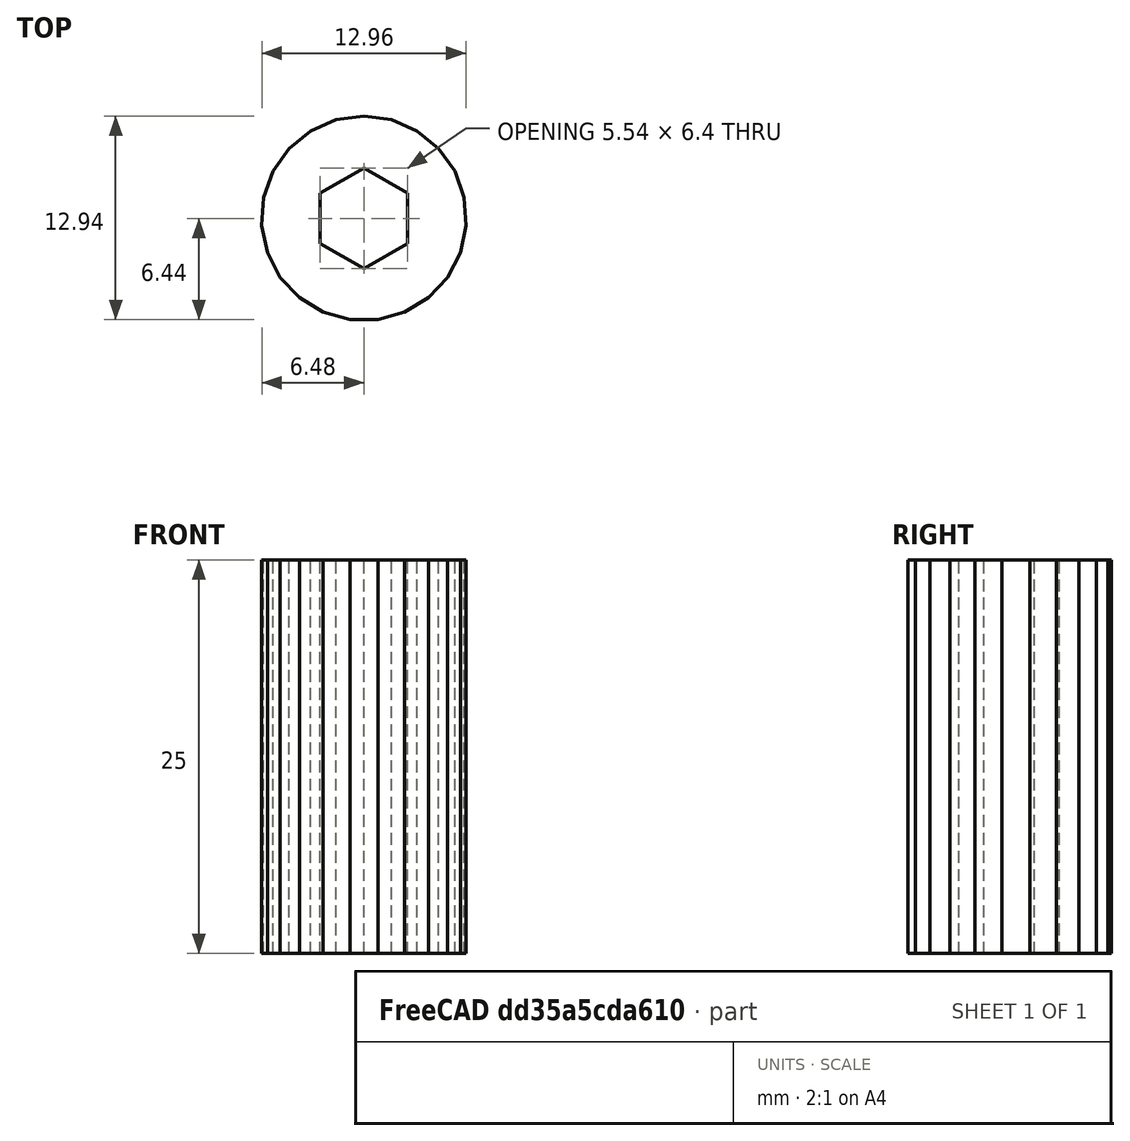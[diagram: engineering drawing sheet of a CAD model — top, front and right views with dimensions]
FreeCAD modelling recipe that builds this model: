
FCSTD DOCUMENT  (FreeCAD 0.19R24344 (Git))
Label: MicroManipulator_Handle
License: All rights reserved
LicenseURL: http://en.wikipedia.org/wiki/All_rights_reserved
objects: Sketcher::SketchObject×1, PartDesign::Pad×1, PartDesign::CoordinateSystem×1, PartDesign::Body×1
note: 5 computed .brp shape members not serialized (recipe doc carries the construction recipe); baked Part::Feature solids carry a one-line shape summary decoded from their .brp

FEATURE [Sketcher::SketchObject] Sketch
  FullyConstrained = true
  MapMode = 5
  Support = -> [XY_Plane]
  sketch-geometry (31):
    g0: LineSegment StartX=2.77128 StartY=-1.6 StartZ=0 EndX=2.77128 EndY=1.6 EndZ=0
    g1: LineSegment StartX=2.77128 StartY=1.6 StartZ=0 EndX=0 EndY=3.2 EndZ=0
    g2: LineSegment StartX=0 StartY=3.2 StartZ=0 EndX=-2.77128 EndY=1.6 EndZ=0
    g3: LineSegment StartX=-2.77128 StartY=1.6 StartZ=0 EndX=-2.77128 EndY=-1.6 EndZ=0
    g4: LineSegment StartX=-2.77128 StartY=-1.6 StartZ=0 EndX=0 EndY=-3.2 EndZ=0
    g5: LineSegment StartX=0 StartY=-3.2 StartZ=0 EndX=2.77128 EndY=-1.6 EndZ=0
    g6: Circle CenterX=0 CenterY=0 CenterZ=0 NormalX=0 NormalY=0 NormalZ=1 AngleXU=0 Radius=3.2
    g7: LineSegment StartX=4.75043 StartY=4.4366 StartZ=0 EndX=3.3773 EndY=5.55373 EndZ=0
    g8: LineSegment StartX=3.3773 StartY=5.55373 StartZ=0 EndX=1.75368 EndY=6.25896 EndZ=0
    g9: LineSegment StartX=1.75368 StartY=6.25896 StartZ=0 EndX=0 EndY=6.5 EndZ=0
    g10: LineSegment StartX=0 StartY=6.5 StartZ=0 EndX=-1.75368 EndY=6.25896 EndZ=0
    g11: LineSegment StartX=-1.75368 StartY=6.25896 StartZ=0 EndX=-3.3773 EndY=5.55373 EndZ=0
    g12: LineSegment StartX=-3.3773 StartY=5.55373 StartZ=0 EndX=-4.75043 EndY=4.4366 EndZ=0
    g13: LineSegment StartX=-4.75043 StartY=4.4366 StartZ=0 EndX=-5.77125 EndY=2.99042 EndZ=0
    g14: LineSegment StartX=-5.77125 StartY=2.99042 StartZ=0 EndX=-6.36405 EndY=1.32246 EndZ=0
    g15: LineSegment StartX=-6.36405 StartY=1.32246 StartZ=0 EndX=-6.48485 EndY=-0.443576 EndZ=0
    g16: LineSegment StartX=-6.48485 StartY=-0.443576 StartZ=0 EndX=-6.1247 EndY=-2.17672 EndZ=0
    g17: LineSegment StartX=-6.1247 StartY=-2.17672 StartZ=0 EndX=-5.3103 EndY=-3.74842 EndZ=0
    g18: LineSegment StartX=-5.3103 StartY=-3.74842 StartZ=0 EndX=-4.10207 EndY=-5.04212 EndZ=0
    g19: LineSegment StartX=-4.10207 StartY=-5.04212 StartZ=0 EndX=-2.58961 EndY=-5.96187 EndZ=0
    g20: LineSegment StartX=-2.58961 StartY=-5.96187 StartZ=0 EndX=-0.885083 EndY=-6.43946 EndZ=0
    g21: LineSegment StartX=-0.885083 StartY=-6.43946 StartZ=0 EndX=0.885083 EndY=-6.43946 EndZ=0
    g22: LineSegment StartX=0.885083 StartY=-6.43946 StartZ=0 EndX=2.58961 EndY=-5.96187 EndZ=0
    g23: LineSegment StartX=2.58961 StartY=-5.96187 StartZ=0 EndX=4.10207 EndY=-5.04212 EndZ=0
    g24: LineSegment StartX=4.10207 StartY=-5.04212 StartZ=0 EndX=5.3103 EndY=-3.74842 EndZ=0
    g25: LineSegment StartX=5.3103 StartY=-3.74842 StartZ=0 EndX=6.1247 EndY=-2.17672 EndZ=0
    g26: LineSegment StartX=6.1247 StartY=-2.17672 StartZ=0 EndX=6.48485 EndY=-0.443576 EndZ=0
    g27: LineSegment StartX=6.48485 StartY=-0.443576 StartZ=0 EndX=6.36405 EndY=1.32246 EndZ=0
    g28: LineSegment StartX=6.36405 StartY=1.32246 StartZ=0 EndX=5.77125 EndY=2.99042 EndZ=0
    g29: LineSegment StartX=5.77125 StartY=2.99042 StartZ=0 EndX=4.75043 EndY=4.4366 EndZ=0
    g30: Circle CenterX=0 CenterY=0 CenterZ=0 NormalX=0 NormalY=0 NormalZ=1 AngleXU=0 Radius=6.5
  constraints (66):
    c: Coincident(g0,g1)
    c: Coincident(g1,g2)
    c: Coincident(g2,g3)
    c: Coincident(g3,g4)
    c: Coincident(g4,g5)
    c: Coincident(g5,g0)
    c: Equal(g0, g1-g5) x5
    c: PointOnObject(g0,g6)
    c: PointOnObject(g1,g6)
    c: PointOnObject(g2,g6)
    c: PointOnObject(g3,g6)
    c: PointOnObject(g4,g6)
    c: PointOnObject(g5,g6)
    c: Coincident(g6,g-1)
    c: Diameter(g6) = 6.4
    c: Coincident(g7,g8)
    c: Coincident(g8,g9)
    c: Coincident(g9,g10)
    c: Coincident(g10,g11)
    c: Coincident(g11,g12)
    c: Coincident(g12,g13)
    c: Coincident(g13,g14)
    c: Coincident(g14,g15)
    c: Coincident(g15,g16)
    c: Coincident(g16,g17)
    c: Coincident(g17,g18)
    c: Coincident(g18,g19)
    c: Coincident(g19,g20)
    c: Coincident(g20,g21)
    c: Coincident(g21,g22)
    c: Coincident(g22,g23)
    c: Coincident(g23,g24)
    c: Coincident(g24,g25)
    c: Coincident(g25,g26)
    c: Coincident(g26,g27)
    c: Coincident(g27,g28)
    c: Coincident(g28,g29)
    c: Coincident(g29,g7)
    c: Equal(g7, g8-g29) x22
    c: PointOnObject(g7,g30)
    c: PointOnObject(g8,g30)
    c: PointOnObject(g9,g30)
    c: PointOnObject(g10,g30)
    c: PointOnObject(g11,g30)
    c: PointOnObject(g12,g30)
    c: PointOnObject(g13,g30)
    c: PointOnObject(g14,g30)
    c: PointOnObject(g15,g30)
    c: PointOnObject(g16,g30)
    c: PointOnObject(g17,g30)
    c: PointOnObject(g18,g30)
    c: PointOnObject(g19,g30)
    c: PointOnObject(g20,g30)
    c: PointOnObject(g21,g30)
    c: PointOnObject(g22,g30)
    c: PointOnObject(g23,g30)
    c: PointOnObject(g24,g30)
    c: PointOnObject(g25,g30)
    c: PointOnObject(g26,g30)
    c: PointOnObject(g27,g30)
    c: PointOnObject(g28,g30)
    c: PointOnObject(g29,g30)
    c: Coincident(g30,g-1)
    c: Diameter(g30) = 13
    c: Vertical(g1,g-1)
    c: Vertical(g9,g-1)
FEATURE [PartDesign::Pad] Pad
  Direction = (1,1,1)
  Length = 25
  Length2 = 100
  Profile = -> Sketch
  Type = 0
FEATURE [PartDesign::CoordinateSystem] LCS_Handle
  AttacherType = Attacher::AttachEngine3D
  MapMode = 45
  Placement = pos=(0,-3e-16,0) rot=(0,0,1;0.523599rad)
  Support = -> [Pad]
FEATURE [PartDesign::Body] Body  label="Handle"
  Group = -> [Sketch,Pad,LCS_Handle]
  Origin = -> Origin
  Tip = -> Pad
